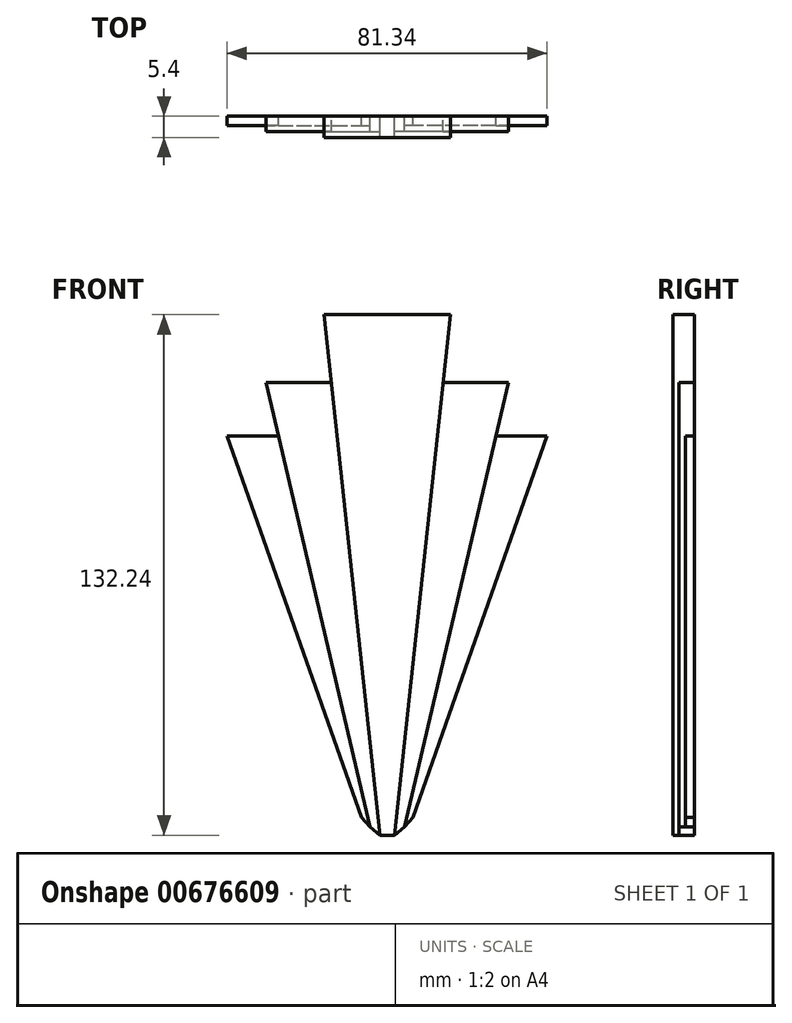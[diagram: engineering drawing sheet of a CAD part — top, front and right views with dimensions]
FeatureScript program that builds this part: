
annotation { "Feature Type Name" : "Feature", "Feature Type Description" : "" }
export const myFeature = defineFeature(function(context is Context, id is Id, definition is map)
    precondition{}
    {
        {
            var Q0;
            Q0=qCreatedBy(makeId("Front.planeOp"),FACE);
            var sketch = newSketch(context, id + "F0", { "sketchPlane" : qUnion([Q0])});
            skLineSegment(sketch, "E0", {"start": v(-16.04, 30.85) * mm, "end": v(-1.83, -101.4) * mm});
            skLineSegment(sketch, "E1.MirrorCS", {"start": v(16.04, 30.85) * mm, "end": v(1.83, -101.4) * mm});
            skLineSegment(sketch, "E2", {"start": v(-1.83, -101.4) * mm, "end": v(1.83, -101.4) * mm});
            skPoint(sketch, "E3.start.orphan", {"position": v(16.04, 30.85) * mm});
            skLineSegment(sketch, "E4", {"start": v(-16.04, 30.85) * mm, "end": v(16.04, 30.85) * mm});
            skLineSegment(sketch, "E5", {"start": v(-14.19, 13.58) * mm, "end": v(-30.8, 13.58) * mm});
            skLineSegment(sketch, "E6.MirrorCS", {"start": v(14.19, 13.58) * mm, "end": v(30.8, 13.58) * mm});
            skLineSegment(sketch, "E7", {"start": v(-30.8, 13.58) * mm, "end": v(-4.4, -99.3) * mm});
            skLineSegment(sketch, "E8", {"start": v(-27.62, 0) * mm, "end": v(-40.67, 0) * mm});
            skLineSegment(sketch, "E9", {"start": v(-40.67, 0) * mm, "end": v(-6.53, -96.86) * mm});
            skLineSegment(sketch, "E10.MirrorCS", {"start": v(30.8, 13.58) * mm, "end": v(4.4, -99.3) * mm});
            skLineSegment(sketch, "E11.MirrorCS", {"start": v(27.62, 0) * mm, "end": v(40.67, 0) * mm});
            skLineSegment(sketch, "E12.MirrorCS", {"start": v(40.67, 0) * mm, "end": v(6.53, -96.86) * mm});
            skLineSegment(sketch, "E13.MirrorCS", {"start": v(16.04, 30.85) * mm, "end": v(-16.04, 30.85) * mm});
            skLineSegment(sketch, "E14", {"start": v(-6.53, -96.86) * mm, "end": v(-4.4, -99.3) * mm});
            skLineSegment(sketch, "E15", {"start": v(-4.4, -99.3) * mm, "end": v(-1.83, -101.4) * mm});
            skLineSegment(sketch, "E16.MirrorCS", {"start": v(6.53, -96.86) * mm, "end": v(4.4, -99.3) * mm});
            skLineSegment(sketch, "E17.MirrorCS", {"start": v(4.4, -99.3) * mm, "end": v(1.83, -101.4) * mm});
            skSolve(sketch);
        }
        {
            var Q0;
            {var subQ3=sQuery(id+"F0.wireOp",EDGE,"E2");Q0=makeQuery(id+"F0.imprint","IMPRINT",FACE,{"disambiguationData":[TD([[makeQuery(id+"F0.imprint","IMPRINT",EDGE,{"derivedFrom":subQ3}),1.0]])]});}
            extrude(context, id + "F1", {"entities" : qUnion([Q0]), "depth" : 5.4 * mm, "offsetDistance" : 25 * mm});
        }
        {
            var Q0;
            {var subQ1=sQuery(id+"F0.wireOp",EDGE,"E5");Q0=makeQuery(id+"F0.imprint","IMPRINT",FACE,{"disambiguationData":[TD([[makeQuery(id+"F0.imprint","IMPRINT",EDGE,{"derivedFrom":subQ1}),1.0]])]});}
            extrude(context, id + "F2", {"entities" : qUnion([Q0]), "depth" : 3.9 * mm, "offsetDistance" : 25 * mm});
        }
        {
            var Q0;
            {var subQ4=sQuery(id+"F0.wireOp",EDGE,"E6.MirrorCS");Q0=makeQuery(id+"F0.imprint","IMPRINT",FACE,{"disambiguationData":[TD([[makeQuery(id+"F0.imprint","IMPRINT",EDGE,{"derivedFrom":subQ4}),-1.0]])]});}
            extrude(context, id + "F3", {"entities" : qUnion([Q0]), "depth" : 3.9 * mm, "offsetDistance" : 25 * mm});
        }
        {
            var Q0;
            {var subQ2=sQuery(id+"F0.wireOp",EDGE,"E8");Q0=makeQuery(id+"F0.imprint","IMPRINT",FACE,{"disambiguationData":[TD([[makeQuery(id+"F0.imprint","IMPRINT",EDGE,{"derivedFrom":subQ2}),1.0]])]});}
            extrude(context, id + "F4", {"entities" : qUnion([Q0]), "operationType" : NewBodyOperationType.ADD, "depth" : 2.3 * mm, "offsetDistance" : 25 * mm});
        }
        {
            var Q0;
            {var subQ2=sQuery(id+"F0.wireOp",EDGE,"E11.MirrorCS");Q0=makeQuery(id+"F0.imprint","IMPRINT",FACE,{"disambiguationData":[TD([[makeQuery(id+"F0.imprint","IMPRINT",EDGE,{"derivedFrom":subQ2}),-1.0]])]});}
            extrude(context, id + "F5", {"entities" : qUnion([Q0]), "operationType" : NewBodyOperationType.ADD, "depth" : 2.3 * mm, "offsetDistance" : 25 * mm});
        }
    });
